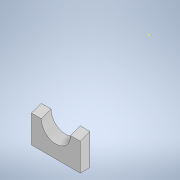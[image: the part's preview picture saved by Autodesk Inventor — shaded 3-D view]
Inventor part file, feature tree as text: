
AUTODESK INVENTOR PART (.ipt)
format: ipt  version: 2021 (Build 250183000, 183)  size: 189,440 bytes
history: native  units: mm
features: sketch x12, extrude x9, plane x2, sweep x1
ambient origin geometry x8: Origin, YZ Plane, XZ Plane, XY Plane, X Axis, Y Axis, Z Axis, Center Point
bodies: Solid1 (feature_tree)
feature tree (24):
  extrude  "Extrusion1"  Depth=25.0mm
  extrude  "Extrusion3"  Depth=12.5mm
  extrude  "Extrusion4"  Depth=10.0mm
  extrude  "Extrusion5"  Depth=25.0mm
  sketch  "Sketch6"  dims[d15=10.0mm d16=0.0mm d18=15.0mm]
  plane  "Work Plane1"
  sweep  "Sweep1"
  sketch  "Sketch9"  dims[d22=15.0mm d23=17.0mm]
  extrude  "Extrusion6"  Depth=10.0mm
  extrude  "Extrusion7"  Depth=17.0mm
  extrude  "Extrusion8"  [1 undecoded]
  plane  "Work Plane2"
  extrude  "Extrusion10"  Depth=8.5mm
  extrude  "Extrusion11"  Depth=25.0mm
  sketch  "Sketch1"  dims[d0=25.0mm d1=50.0mm]
  sketch  "Sketch3"  dims[d2=12.5mm d3=12.5mm]
  sketch  "Sketch4"  dims[d4=10.0mm d5=0.0mm d11=15.0mm]
  sketch  "Sketch5"  dims[d12=15.0mm d13=0.0mm d14=25.0mm]
  sketch  "Sketch8"  dims[d19=10.0mm d20=0.0mm d21=30.0mm]
  sketch  "Sketch10"  dims[d24=17.0mm d25=-12.5mm]
  sketch  "Sketch11"  dims[d26=3.490659mm d27=8.5mm]
  sketch  "Sketch12"  dims[d28=0.0mm d29=0.0mm d32=25.0mm]
  sketch  "Sketch15"  dims[d33=10.0mm d34=0.0mm]
  sketch  "Sketch16"  dims[d35=10.0mm d36=0.0mm d37=5.0mm d38=10.0mm d39=0.0mm d40=-43.75mm d43=3.0mm d44=0.0mm d45=3.0mm d46=0.0mm]
note: 1 required parameter value undecoded (feature->parameter linkage not recoverable at this tier; creation-order binding heuristic only, values carry confidence <= 0.55)
